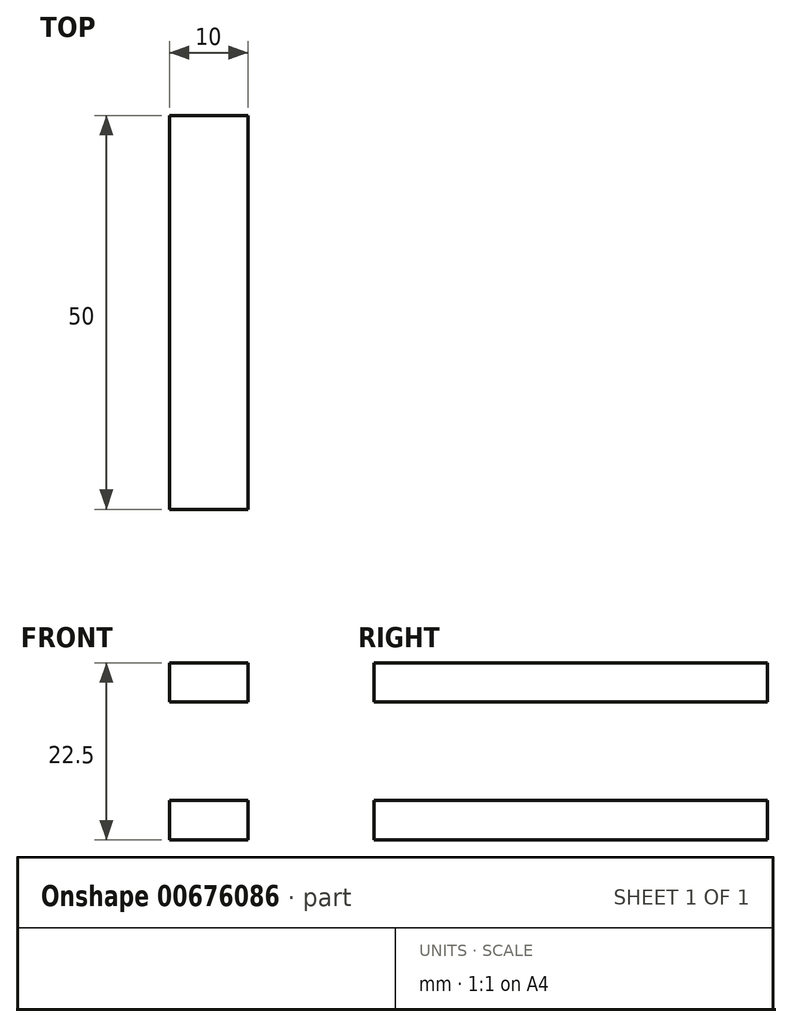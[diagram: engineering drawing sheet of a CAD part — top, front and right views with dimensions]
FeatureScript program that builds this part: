
annotation { "Feature Type Name" : "Feature", "Feature Type Description" : "" }
export const myFeature = defineFeature(function(context is Context, id is Id, definition is map)
    precondition{}
    {
        {
            var Q0;
            Q0=qCreatedBy(makeId("Front.planeOp"),FACE);
            var sketch = newSketch(context, id + "F0", { "sketchPlane" : qUnion([Q0])});
            skLineSegment(sketch, "E0.bottom", {"start": v(-2.5, 8.75) * mm, "end": v(2.5, 8.75) * mm});
            skLineSegment(sketch, "E0.top", {"start": v(-2.5, -8.75) * mm, "end": v(2.5, -8.75) * mm});
            skLineSegment(sketch, "E0.left", {"start": v(-2.5, 8.75) * mm, "end": v(-2.5, -8.75) * mm});
            skLineSegment(sketch, "E0.right", {"start": v(2.5, 8.75) * mm, "end": v(2.5, -8.75) * mm});
            skPoint(sketch, "E0.middle", {"position": v(0, 0) * mm});
            skLineSegment(sketch, "E1.bottom", {"start": v(-5, 11.25) * mm, "end": v(5, 11.25) * mm});
            skLineSegment(sketch, "E1.top", {"start": v(-5, 6.25) * mm, "end": v(5, 6.25) * mm});
            skLineSegment(sketch, "E1.left", {"start": v(-5, 11.25) * mm, "end": v(-5, 6.25) * mm});
            skLineSegment(sketch, "E1.right", {"start": v(5, 11.25) * mm, "end": v(5, 6.25) * mm});
            skPoint(sketch, "E1.middle", {"position": v(0, 8.75) * mm});
            skLineSegment(sketch, "E2.bottom", {"start": v(-5, -11.25) * mm, "end": v(5, -11.25) * mm});
            skLineSegment(sketch, "E2.top", {"start": v(-5, -6.25) * mm, "end": v(5, -6.25) * mm});
            skLineSegment(sketch, "E2.left", {"start": v(-5, -11.25) * mm, "end": v(-5, -6.25) * mm});
            skLineSegment(sketch, "E2.right", {"start": v(5, -11.25) * mm, "end": v(5, -6.25) * mm});
            skPoint(sketch, "E2.middle", {"position": v(0, -8.75) * mm});
            skSolve(sketch);
        }
        {
            var Q0;
            {var subQ1=sQuery(id+"F0.wireOp",EDGE,"E0.bottom");Q0=makeQuery(id+"F0.imprint","IMPRINT",FACE,{"disambiguationData":[TD([[makeQuery(id+"F0.imprint","IMPRINT",EDGE,{"derivedFrom":subQ1}),1.0]])]});}
            var Q1;
            {var subQ1=sQuery(id+"F0.wireOp",EDGE,"E0.top");Q1=makeQuery(id+"F0.imprint","IMPRINT",FACE,{"disambiguationData":[TD([[makeQuery(id+"F0.imprint","IMPRINT",EDGE,{"derivedFrom":subQ1}),-1.0]])]});}
            var Q2;
            {var subQ0=sQuery(id+"F0.wireOp",EDGE,"E0.bottom");Q2=makeQuery(id+"F0.imprint","IMPRINT",FACE,{"disambiguationData":[TD([[makeQuery(id+"F0.imprint","IMPRINT",EDGE,{"derivedFrom":subQ0}),-1.0]])]});}
            var Q3;
            {var subQ0=sQuery(id+"F0.wireOp",EDGE,"E0.top");Q3=makeQuery(id+"F0.imprint","IMPRINT",FACE,{"disambiguationData":[TD([[makeQuery(id+"F0.imprint","IMPRINT",EDGE,{"derivedFrom":subQ0}),1.0]])]});}
            extrude(context, id + "F1", {"entities" : qUnion([Q0, Q1, Q2, Q3]), "endBound" : BoundingType.SYMMETRIC, "depth" : 50 * mm, "offsetDistance" : 25.4 * mm});
        }
    });
